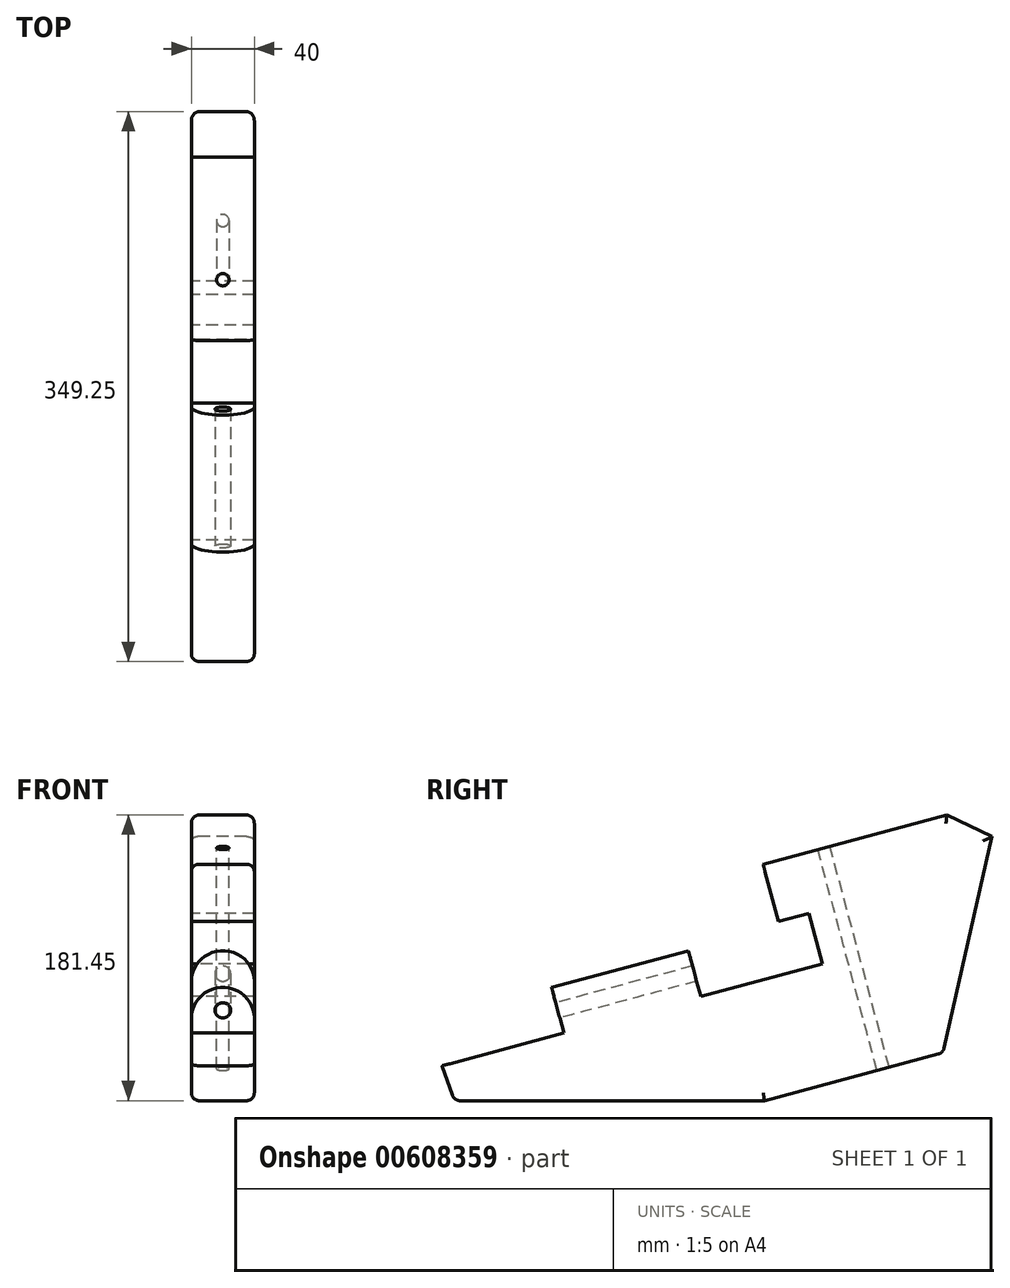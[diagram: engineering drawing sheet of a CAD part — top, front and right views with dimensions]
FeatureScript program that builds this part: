
annotation { "Feature Type Name" : "Feature", "Feature Type Description" : "" }
export const myFeature = defineFeature(function(context is Context, id is Id, definition is map)
    precondition{}
    {
        {
            var Q0;
            Q0=qCreatedBy(makeId("Right.planeOp"),FACE);
            var sketch = newSketch(context, id + "F0", { "sketchPlane" : qUnion([Q0])});
            skLineSegment(sketch, "E0", {"start": v(-64.97, 0) * mm, "end": v(81.53, 39.26) * mm, "construction": true});
            skLineSegment(sketch, "E1", {"start": v(-31.55, 8.96) * mm, "end": v(-23.78, -20.02) * mm});
            skLineSegment(sketch, "E2", {"start": v(-23.78, -20.02) * mm, "end": v(-101.06, -40.73) * mm});
            skLineSegment(sketch, "E3", {"start": v(-31.55, 8.96) * mm, "end": v(55.39, 32.25) * mm});
            skLineSegment(sketch, "E4", {"start": v(55.39, 32.25) * mm, "end": v(63.15, 3.27) * mm});
            skLineSegment(sketch, "E5", {"start": v(63.15, 3.27) * mm, "end": v(140.43, 23.98) * mm});
            skLineSegment(sketch, "E6", {"start": v(-101.06, -40.73) * mm, "end": v(68.91, 4.82) * mm, "construction": true});
            skLineSegment(sketch, "E7", {"start": v(-93.38, -62.93) * mm, "end": v(103.56, -62.93) * mm});
            skLineSegment(sketch, "E8", {"start": v(103.56, -62.93) * mm, "end": v(217.06, -32.52) * mm});
            skLineSegment(sketch, "E9", {"start": v(-101.06, -40.73) * mm, "end": v(-93.38, -62.93) * mm});
            skLineSegment(sketch, "E10", {"start": v(102.77, 87.25) * mm, "end": v(219.45, 118.52) * mm});
            skLineSegment(sketch, "E11", {"start": v(219.45, 118.52) * mm, "end": v(248.2, 104.81) * mm});
            skLineSegment(sketch, "E12", {"start": v(248.2, 104.81) * mm, "end": v(217.06, -32.52) * mm});
            skLineSegment(sketch, "E13", {"start": v(102.77, 87.25) * mm, "end": v(112.53, 50.8) * mm});
            skLineSegment(sketch, "E14", {"start": v(112.53, 50.8) * mm, "end": v(131.85, 55.98) * mm});
            skLineSegment(sketch, "E15", {"start": v(131.85, 55.98) * mm, "end": v(140.43, 23.98) * mm});
            skSolve(sketch);
        }
        {
            var Q0;
            Q0=makeQuery(id+"F0.imprint","IMPRINT",FACE,{"disambiguationData":[TD([[makeQuery(id+"F0.imprint","IMPRINT",EDGE,{"derivedFrom":sQuery(id+"F0.wireOp",EDGE,"E1")}),1.0]])]});
            extrude(context, id + "F1", {"entities" : qUnion([Q0]), "endBound" : BoundingType.SYMMETRIC, "depth" : 40 * mm, "offsetDistance" : 25 * mm});
        }
        {
            var Q0;
            Q0=makeQuery(id+"F1.opExtrude","SWEPT_FACE",FACE,{"disambiguationData":[OSD([sQuery(id+"F0.wireOp",EDGE,"E1")])]});
            var sketch = newSketch(context, id + "F2", { "sketchPlane" : qUnion([Q0])});
            skCircle(sketch, "E16", {"center": v(0, 1.82) * mm, "radius": 5 * mm});
            skPoint(sketch, "E16.centerSnap0", {"position": v(-20, 1.82) * mm});
            skSolve(sketch);
        }
        {
            var Q0;
            Q0=sQuery(id+"F2.wireOp",VERTEX,"E16.center");
            var Q1;
            Q1=makeQuery(id+"F1.opExtrude","SWEPT_BODY",BODY,{"disambiguationData":[OSD([sQuery(id+"F0.wireOp",EDGE,"E1"),sQuery(id+"F0.wireOp",EDGE,"E2"),sQuery(id+"F0.wireOp",EDGE,"E3"),sQuery(id+"F0.wireOp",EDGE,"E4"),sQuery(id+"F0.wireOp",EDGE,"E5"),sQuery(id+"F0.wireOp",EDGE,"FHwII1ot-Ncys-d2CP-vKDi-uwtZ2G2WRNRB"),sQuery(id+"F0.wireOp",EDGE,"E7"),sQuery(id+"F0.wireOp",EDGE,"E8"),sQuery(id+"F0.wireOp",EDGE,"tCdSFkAt-Vwn5-Bogr-ycq3-b7GdUqY8maBw"),sQuery(id+"F0.wireOp",EDGE,"TEKWCcrC-938w-F7jd-rMet-1zSs6PMw3WKi"),sQuery(id+"F0.wireOp",EDGE,"v7jpS4dM-Vr38-ctDQ-GzjW-VMAKQeBi5pG9"),sQuery(id+"F0.wireOp",EDGE,"8XV3AbKs-6CBt-QYnA-7GSD-IqfxNcAQh4Ob")])]});
            hole(context, id + "F3", {"style" : HoleStyle.SIMPLE, "endStyle" : HoleEndStyle.BLIND, "holeDiameter" : 10 * mm, "majorDiameter" : 5 * mm, "holeDepth" : 90 * mm, "isTappedThrough" : true, "tappedDepth" : 12 * mm, "tapClearance" : 3, "locations" : qUnion([Q0]), "scope" : qUnion([Q1])});
        }
        {
            var Q0;
            Q0=makeQuery(id+"F1.opExtrude","CAP_EDGE",EDGE,{"disambiguationData":[OSD([sQuery(id+"F0.wireOp",EDGE,"E3")])],"isStart":false});
            var Q1;
            Q1=makeQuery(id+"F1.opExtrude","CAP_EDGE",EDGE,{"disambiguationData":[OSD([sQuery(id+"F0.wireOp",EDGE,"E3")])],"isStart":true});
            fillet(context, id + "F4", {"entities" : qUnion([Q0, Q1]), "radius" : 20 * mm, "tangentPropagation" : true, "allowEdgeOverflow" : false});
        }
        {
            var Q0;
            Q0=makeQuery(id+"F1.opExtrude","CAP_EDGE",EDGE,{"disambiguationData":[OSD([sQuery(id+"F0.wireOp",EDGE,"E9")])],"isStart":true});
            var Q1;
            Q1=makeQuery(id+"F1.opExtrude","CAP_EDGE",EDGE,{"disambiguationData":[OSD([sQuery(id+"F0.wireOp",EDGE,"E9")])],"isStart":false});
            var Q2;
            Q2=makeQuery(id+"F1.opExtrude","SWEPT_EDGE",EDGE,{"disambiguationData":[OSD([sQuery(id+"F0.wireOp",EDGE,"E7"),sQuery(id+"F0.wireOp",EDGE,"E9")])]});
            var Q3;
            Q3=makeQuery(id+"F1.opExtrude","CAP_EDGE",EDGE,{"disambiguationData":[OSD([sQuery(id+"F0.wireOp",EDGE,"E7")])],"isStart":false});
            var Q4;
            Q4=makeQuery(id+"F1.opExtrude","CAP_EDGE",EDGE,{"disambiguationData":[OSD([sQuery(id+"F0.wireOp",EDGE,"E7")])],"isStart":true});
            var Q5;
            Q5=makeQuery(id+"F1.opExtrude","CAP_EDGE",EDGE,{"disambiguationData":[OSD([sQuery(id+"F0.wireOp",EDGE,"E8")])],"isStart":false});
            var Q6;
            Q6=makeQuery(id+"F1.opExtrude","CAP_EDGE",EDGE,{"disambiguationData":[OSD([sQuery(id+"F0.wireOp",EDGE,"E8")])],"isStart":true});
            var Q7;
            Q7=makeQuery(id+"F1.opExtrude","SWEPT_EDGE",EDGE,{"disambiguationData":[OSD([sQuery(id+"F0.wireOp",EDGE,"E8"),sQuery(id+"F0.wireOp",EDGE,"E12")])]});
            var Q8;
            Q8=makeQuery(id+"F1.opExtrude","CAP_EDGE",EDGE,{"disambiguationData":[OSD([sQuery(id+"F0.wireOp",EDGE,"E12")])],"isStart":false});
            var Q9;
            Q9=makeQuery(id+"F1.opExtrude","CAP_EDGE",EDGE,{"disambiguationData":[OSD([sQuery(id+"F0.wireOp",EDGE,"E12")])],"isStart":true});
            var Q10;
            Q10=makeQuery(id+"F1.opExtrude","CAP_EDGE",EDGE,{"disambiguationData":[OSD([sQuery(id+"F0.wireOp",EDGE,"E11")])],"isStart":true});
            var Q11;
            Q11=makeQuery(id+"F1.opExtrude","CAP_EDGE",EDGE,{"disambiguationData":[OSD([sQuery(id+"F0.wireOp",EDGE,"E11")])],"isStart":false});
            var Q12;
            Q12=makeQuery(id+"F1.opExtrude","CAP_EDGE",EDGE,{"disambiguationData":[OSD([sQuery(id+"F0.wireOp",EDGE,"E10")])],"isStart":false});
            var Q13;
            Q13=makeQuery(id+"F1.opExtrude","CAP_EDGE",EDGE,{"disambiguationData":[OSD([sQuery(id+"F0.wireOp",EDGE,"E10")])],"isStart":true});
            fillet(context, id + "F5", {"entities" : qUnion([Q0, Q1, Q2, Q3, Q4, Q5, Q6, Q7, Q8, Q9, Q10, Q11, Q12, Q13]), "radius" : 5 * mm, "tangentPropagation" : true, "allowEdgeOverflow" : false});
        }
        {
            var Q0;
            Q0=makeQuery(id+"F1.opExtrude","SWEPT_FACE",FACE,{"disambiguationData":[OSD([sQuery(id+"F0.wireOp",EDGE,"E10")])]});
            var sketch = newSketch(context, id + "F6", { "sketchPlane" : qUnion([Q0])});
            skCircle(sketch, "E17", {"center": v(0, 161.85) * mm, "radius": 4 * mm});
            skSolve(sketch);
        }
        {
            var Q0;
            Q0=sQuery(id+"F6.wireOp",VERTEX,"E17.center");
            var Q1;
            Q1=makeQuery(id+"F1.opExtrude","SWEPT_BODY",BODY,{"disambiguationData":[OSD([sQuery(id+"F0.wireOp",EDGE,"E1"),sQuery(id+"F0.wireOp",EDGE,"E2"),sQuery(id+"F0.wireOp",EDGE,"E3"),sQuery(id+"F0.wireOp",EDGE,"E4"),sQuery(id+"F0.wireOp",EDGE,"E5"),sQuery(id+"F0.wireOp",EDGE,"E7"),sQuery(id+"F0.wireOp",EDGE,"E8"),sQuery(id+"F0.wireOp",EDGE,"8XV3AbKs-6CBt-QYnA-7GSD-IqfxNcAQh4Ob"),sQuery(id+"F0.wireOp",EDGE,"E9"),sQuery(id+"F0.wireOp",EDGE,"E10"),sQuery(id+"F0.wireOp",EDGE,"E11"),sQuery(id+"F0.wireOp",EDGE,"E12")])]});
            hole(context, id + "F7", {"style" : HoleStyle.SIMPLE, "endStyle" : HoleEndStyle.THROUGH, "holeDiameter" : 8 * mm, "majorDiameter" : 5 * mm, "isTappedThrough" : true, "tappedDepth" : 12 * mm, "tapClearance" : 3, "locations" : qUnion([Q0]), "scope" : qUnion([Q1])});
        }
    });
